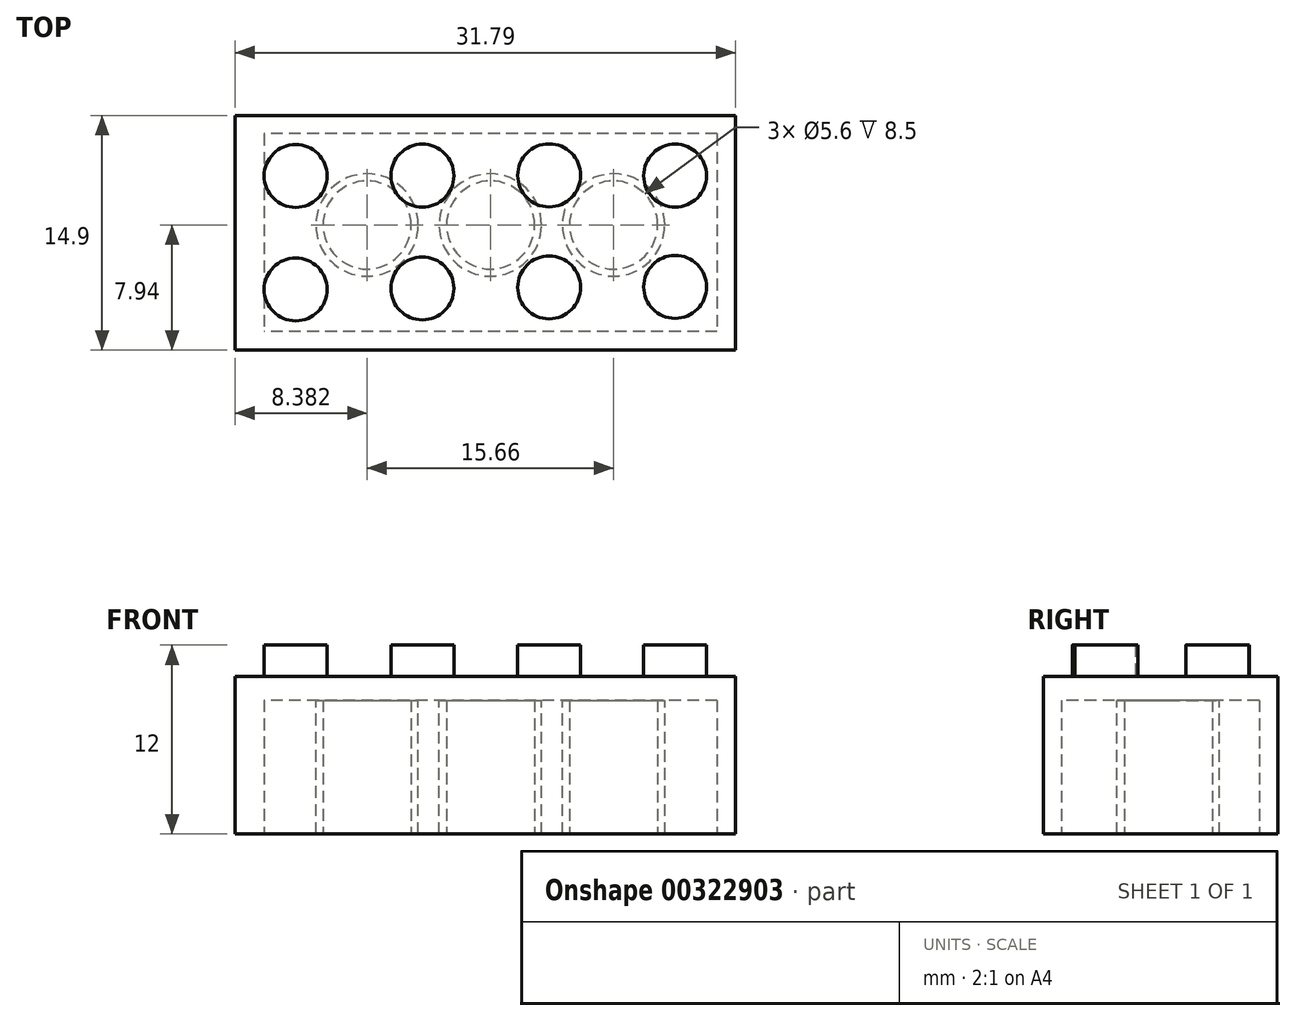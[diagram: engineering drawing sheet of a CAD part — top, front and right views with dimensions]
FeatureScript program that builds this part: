
annotation { "Feature Type Name" : "Feature", "Feature Type Description" : "" }
export const myFeature = defineFeature(function(context is Context, id is Id, definition is map)
    precondition{}
    {
        {
            var Q0;
            Q0=qCreatedBy(makeId("Front.planeOp"),FACE);
            var sketch = newSketch(context, id + "F0", { "sketchPlane" : qUnion([Q0])});
            skLineSegment(sketch, "E0.bottom", {"start": v(15.56, 5) * mm, "end": v(-16.23, 5) * mm});
            skLineSegment(sketch, "E0.top", {"start": v(15.56, -5) * mm, "end": v(-16.23, -5) * mm});
            skLineSegment(sketch, "E0.left", {"start": v(15.56, 5) * mm, "end": v(15.56, -5) * mm});
            skLineSegment(sketch, "E0.right", {"start": v(-16.23, 5) * mm, "end": v(-16.23, -5) * mm});
            skPoint(sketch, "E0.middle", {"position": v(-0.33, 0) * mm});
            skSolve(sketch);
        }
        {
            var Q0;
            Q0 = qSketchRegion(id + "F0", true);
            extrude(context, id + "F1", {"entities" : qUnion([Q0]), "depth" : 14.9 * mm});
        }
        {
            var Q0;
            Q0=makeQuery(id+"F1.opExtrude","SWEPT_FACE",FACE,{"disambiguationData":[OSD([sQuery(id+"F0.wireOp",EDGE,"E0.top")])]});
            var sketch = newSketch(context, id + "F2", { "sketchPlane" : qUnion([Q0])});
            skLineSegment(sketch, "E1.bottom", {"start": v(14.4, 1.17) * mm, "end": v(-14.4, 1.17) * mm});
            skLineSegment(sketch, "E1.top", {"start": v(14.4, 13.73) * mm, "end": v(-14.4, 13.73) * mm});
            skLineSegment(sketch, "E1.left", {"start": v(14.4, 1.17) * mm, "end": v(14.4, 13.73) * mm});
            skLineSegment(sketch, "E1.right", {"start": v(-14.4, 1.17) * mm, "end": v(-14.4, 13.73) * mm});
            skPoint(sketch, "E1.middle", {"position": v(0, 7.45) * mm});
            skSolve(sketch);
        }
        {
            var Q0;
            Q0 = qSketchRegion(id + "F2", true);
            extrude(context, id + "F3", {"entities" : qUnion([Q0]), "operationType" : NewBodyOperationType.REMOVE, "oppositeDirection" : true, "depth" : 8.5 * mm});
        }
        {
            var Q0;
            Q0=makeQuery(id+"F1.opExtrude","SWEPT_FACE",FACE,{"disambiguationData":[OSD([sQuery(id+"F0.wireOp",EDGE,"E0.bottom")])]});
            var sketch = newSketch(context, id + "F4", { "sketchPlane" : qUnion([Q0])});
            skCircle(sketch, "E2", {"center": v(-12.38, -3.85) * mm, "radius": 2 * mm});
            skCircle(sketch, "E3.1.0.0", {"center": v(-4.33, -3.83) * mm, "radius": 2 * mm});
            skCircle(sketch, "E3.2.0.0", {"center": v(3.72, -3.8) * mm, "radius": 2 * mm});
            skLineSegment(sketch, "E3.direction1", {"start": v(-12.38, -3.85) * mm, "end": v(-4.33, -3.83) * mm, "construction": true});
            skCircle(sketch, "E4.1.0.0", {"center": v(11.72, -3.82) * mm, "radius": 2 * mm});
            skLineSegment(sketch, "E4.direction1", {"start": v(3.72, -3.8) * mm, "end": v(11.72, -3.82) * mm, "construction": true});
            skCircle(sketch, "E5.1.0.0", {"center": v(-12.38, -11.06) * mm, "radius": 2 * mm});
            skLineSegment(sketch, "E5.direction1", {"start": v(-12.38, -3.84) * mm, "end": v(-12.38, -11.06) * mm, "construction": true});
            skCircle(sketch, "E6.1.0.0", {"center": v(-4.33, -11) * mm, "radius": 2 * mm});
            skCircle(sketch, "E6.2.0.0", {"center": v(3.72, -10.93) * mm, "radius": 2 * mm});
            skLineSegment(sketch, "E6.direction1", {"start": v(-12.38, -11.06) * mm, "end": v(-4.33, -11) * mm, "construction": true});
            skCircle(sketch, "E7.1.0.0", {"center": v(11.72, -10.9) * mm, "radius": 2 * mm});
            skLineSegment(sketch, "E7.direction1", {"start": v(3.72, -10.93) * mm, "end": v(11.72, -10.9) * mm, "construction": true});
            skSolve(sketch);
        }
        {
            var Q0;
            Q0 = qSketchRegion(id + "F4", true);
            extrude(context, id + "F5", {"entities" : qUnion([Q0]), "operationType" : NewBodyOperationType.ADD, "depth" : 2 * mm});
        }
        {
            var Q0;
            Q0=makeQuery(id+"F3.boolean.opBoolean","COPY",FACE,{"derivedFrom":makeQuery(id+"F3.opExtrude","CAP_FACE",FACE,{"disambiguationData":[OSD([sQuery(id+"F2.wireOp",EDGE,"E1.bottom"),sQuery(id+"F2.wireOp",EDGE,"E1.top"),sQuery(id+"F2.wireOp",EDGE,"E1.left"),sQuery(id+"F2.wireOp",EDGE,"E1.right")])],"isStart":false})});
            var sketch = newSketch(context, id + "F6", { "sketchPlane" : qUnion([Q0])});
            skCircle(sketch, "E8", {"center": v(-0.02, 6.96) * mm, "radius": 3.25 * mm});
            skCircle(sketch, "E9", {"center": v(-7.85, 6.96) * mm, "radius": 3.25 * mm});
            skCircle(sketch, "E10", {"center": v(7.81, 6.96) * mm, "radius": 3.25 * mm});
            skSolve(sketch);
        }
        {
            var Q0;
            Q0 = qSketchRegion(id + "F6", true);
            extrude(context, id + "F7", {"entities" : qUnion([Q0]), "operationType" : NewBodyOperationType.ADD, "depth" : 8.5 * mm});
        }
        {
            var Q0;
            Q0=makeQuery(id+"F7.opExtrude","CAP_FACE",FACE,{"disambiguationData":[OSD([sQuery(id+"F6.wireOp",EDGE,"E9")])],"isStart":false});
            var sketch = newSketch(context, id + "F8", { "sketchPlane" : qUnion([Q0])});
            skCircle(sketch, "E11", {"center": v(-7.85, 6.96) * mm, "radius": 2.8 * mm});
            skCircle(sketch, "E12", {"center": v(0, 6.96) * mm, "radius": 2.8 * mm});
            skCircle(sketch, "E13.1.0.0", {"center": v(7.81, 6.96) * mm, "radius": 2.8 * mm});
            skSolve(sketch);
        }
        {
            var Q0;
            Q0 = qSketchRegion(id + "F8", true);
            extrude(context, id + "F9", {"entities" : qUnion([Q0]), "operationType" : NewBodyOperationType.REMOVE, "oppositeDirection" : true, "depth" : 8.5 * mm});
        }
    });
